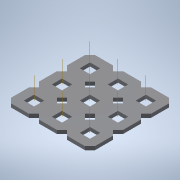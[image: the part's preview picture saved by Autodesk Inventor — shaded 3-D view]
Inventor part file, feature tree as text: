
AUTODESK INVENTOR PART (.ipt)
format: ipt  version: 2020 (Build 240168000, 168)  size: 1,138,688 bytes
history: native  units: in
note: dims shown in document units (in); Inventor stores cm internally (conversion verified against a paired STEP export)
features: other x18, extrude x2, pattern_linear x1, plane x1, split x1, imported_body x1
ambient origin geometry x8: Origin, YZ Plane, XZ Plane, XY Plane, X Axis, Y Axis, Z Axis, Center Point
bodies: Body1 (feature_tree)
feature tree (24):
  other  "Diamond-Pattern"
  other  "Plate"
  extrude  "length cut"  TaperAngle=0.0deg  [1 undecoded]
  extrude  "width cut"  TaperAngle=0.0deg  [1 undecoded]
  other  "constraint axis"
  pattern_linear  "constraint axes"  Spacing1=0.5in  [1 undecoded]
  other  "front plane"
  other  "right plane"
  plane  "Work Plane5"
  split  "Split1"
  imported_body  "Base1"
  other  "length profile"
  other  "width profile"
  other  "Work Point1"
  other  "Work Axis36"
  other  "Work Axis37"
  other  "Work Axis40"
  other  "Work Axis41"
  other  "Work Axis42"
  other  "Work Axis43"
  other  "Work Axis44"
  other  "Work Axis45"
  other  "back plane"
  other  "left plane"
note: 3 required parameter values undecoded (feature->parameter linkage not recoverable at this tier; creation-order binding heuristic only, values carry confidence <= 0.55)
